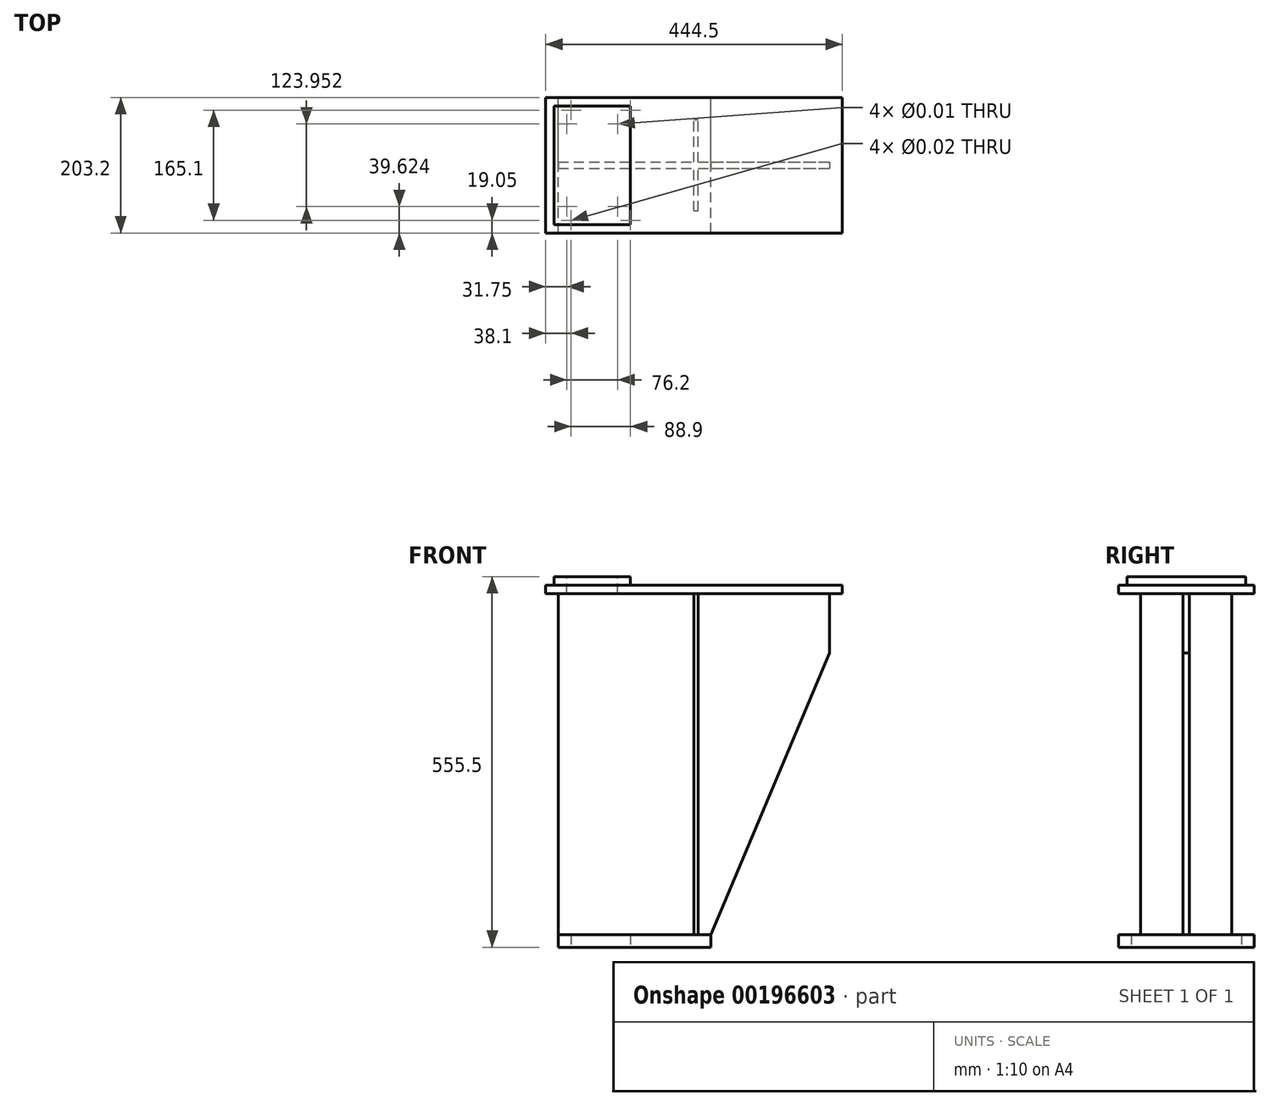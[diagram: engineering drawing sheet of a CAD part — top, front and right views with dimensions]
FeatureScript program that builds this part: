
annotation { "Feature Type Name" : "Feature", "Feature Type Description" : "" }
export const myFeature = defineFeature(function(context is Context, id is Id, definition is map)
    precondition{}
    {
        {
            var Q0;
            Q0=qCreatedBy(makeId("Top.planeOp"),FACE);
            var sketch = newSketch(context, id + "F0", { "sketchPlane" : qUnion([Q0])});
            skLineSegment(sketch, "E0.bottom", {"start": v(-222.25, 101.6) * mm, "end": v(222.25, 101.6) * mm});
            skLineSegment(sketch, "E0.top", {"start": v(-222.25, -101.6) * mm, "end": v(222.25, -101.6) * mm});
            skLineSegment(sketch, "E0.left", {"start": v(-222.25, 101.6) * mm, "end": v(-222.25, -101.6) * mm});
            skLineSegment(sketch, "E0.right", {"start": v(222.25, 101.6) * mm, "end": v(222.25, -101.6) * mm});
            skPoint(sketch, "E0.middle", {"position": v(0, 0) * mm});
            skSolve(sketch);
        }
        {
            var Q0;
            Q0 = qSketchRegion(id + "F0", true);
            extrude(context, id + "F1", {"entities" : qUnion([Q0]), "depth" : 12.7 * mm});
        }
        {
            var Q0;
            Q0=makeQuery(id+"F1.opExtrude","CAP_FACE",FACE,{"disambiguationData":[OSD([sQuery(id+"F0.wireOp",EDGE,"E0.bottom"),sQuery(id+"F0.wireOp",EDGE,"E0.top"),sQuery(id+"F0.wireOp",EDGE,"E0.left"),sQuery(id+"F0.wireOp",EDGE,"E0.right")])],"isStart":false});
            var sketch = newSketch(context, id + "F2", { "sketchPlane" : qUnion([Q0])});
            skLineSegment(sketch, "E1", {"start": v(-249.9, 0) * mm, "end": v(312.08, 0) * mm, "construction": true});
            skPoint(sketch, "E1.endSnap0", {"position": v(-222.25, 0) * mm});
            skLineSegment(sketch, "E2.0", {"start": v(-222.25, 101.6) * mm, "end": v(-222.25, -101.6) * mm, "construction": true});
            skLineSegment(sketch, "E3.0", {"start": v(-152.4, 101.6) * mm, "end": v(-152.4, -101.6) * mm, "construction": true});
            skLineSegment(sketch, "E4.0", {"start": v(-249.9, -88.9) * mm, "end": v(312.08, -88.9) * mm, "construction": true});
            skLineSegment(sketch, "E5.0", {"start": v(-209.55, 101.6) * mm, "end": v(-209.55, -101.6) * mm, "construction": true});
            skLineSegment(sketch, "E6.bottom", {"start": v(-209.55, -88.9) * mm, "end": v(-95.25, -88.9) * mm});
            skLineSegment(sketch, "E6.top", {"start": v(-209.55, 88.9) * mm, "end": v(-95.25, 88.9) * mm});
            skLineSegment(sketch, "E6.left", {"start": v(-209.55, -88.9) * mm, "end": v(-209.55, 88.9) * mm});
            skLineSegment(sketch, "E6.right", {"start": v(-95.25, -88.9) * mm, "end": v(-95.25, 88.9) * mm});
            skSolve(sketch);
        }
        {
            var Q0;
            Q0 = qSketchRegion(id + "F2", true);
            extrude(context, id + "F3", {"entities" : qUnion([Q0]), "operationType" : NewBodyOperationType.ADD, "depth" : 12.7 * mm});
        }
        {
            var Q0;
            Q0=makeQuery(id+"F3.opExtrude","CAP_FACE",FACE,{"disambiguationData":[OSD([sQuery(id+"F2.wireOp",EDGE,"E6.bottom"),sQuery(id+"F2.wireOp",EDGE,"E6.top"),sQuery(id+"F2.wireOp",EDGE,"E6.left"),sQuery(id+"F2.wireOp",EDGE,"E6.right")])],"isStart":false});
            var sketch = newSketch(context, id + "F4", { "sketchPlane" : qUnion([Q0])});
            skLineSegment(sketch, "E7", {"start": v(-266.4, 0) * mm, "end": v(-62.42, 0) * mm, "construction": true});
            skPoint(sketch, "E7.endSnap0", {"position": v(-95.25, 0) * mm});
            skLineSegment(sketch, "E8", {"start": v(-152.4, 88.9) * mm, "end": v(-152.4, -88.9) * mm, "construction": true});
            skLineSegment(sketch, "E9.0", {"start": v(-190.5, 88.9) * mm, "end": v(-190.5, -88.9) * mm, "construction": true});
            skLineSegment(sketch, "E10.0", {"start": v(-266.4, 61.98) * mm, "end": v(-62.42, 61.98) * mm, "construction": true});
            skPoint(sketch, "E11", {"position": v(-190.5, 61.98) * mm});
            skPoint(sketch, "E12.0.1.0", {"position": v(-190.5, -61.98) * mm});
            skPoint(sketch, "E12.1.0.0", {"position": v(-114.3, 61.98) * mm});
            skPoint(sketch, "E12.1.1.0", {"position": v(-114.3, -61.98) * mm});
            skLineSegment(sketch, "E12.direction1", {"start": v(-190.5, 61.98) * mm, "end": v(-114.3, 61.98) * mm, "construction": true});
            skLineSegment(sketch, "E12.direction2", {"start": v(-190.5, 61.98) * mm, "end": v(-190.5, -61.98) * mm, "construction": true});
            skSolve(sketch);
        }
        {
            var Q0;
            Q0=sQuery(id+"F4.wireOp",VERTEX,"E11");
            var Q1;
            Q1=sQuery(id+"F4.wireOp",VERTEX,"E12.1.0.0");
            var Q2;
            Q2=sQuery(id+"F4.wireOp",VERTEX,"E12.1.1.0");
            var Q3;
            Q3=sQuery(id+"F4.wireOp",VERTEX,"E12.0.1.0");
            var Q4;
            Q4=makeQuery(id+"F1.opExtrude","SWEPT_BODY",BODY,{"disambiguationData":[OSD([sQuery(id+"F0.wireOp",EDGE,"E0.bottom"),sQuery(id+"F0.wireOp",EDGE,"E0.top"),sQuery(id+"F0.wireOp",EDGE,"E0.left"),sQuery(id+"F0.wireOp",EDGE,"E0.right")])]});
            hole(context, id + "F5", {"style" : HoleStyle.SIMPLE, "endStyle" : HoleEndStyle.THROUGH, "standardTappedOrClearance" : lookupTablePath({ "standard" : "ANSI", "size" : "3/8 (0.38)", "type" : "Drilled" }), "standardBlindInLast" : lookupTablePath({ "standard" : "ANSI", "size" : "3/8", "type" : "Drilled" }), "holeDiameter" : 3 / 203.2 * mm, "locations" : qUnion([Q0, Q1, Q2, Q3]), "scope" : qUnion([Q4]), "isTappedThrough" : true});
        }
        {
            var Q0;
            Q0=makeQuery(id+"F1.opExtrude","CAP_FACE",FACE,{"disambiguationData":[OSD([sQuery(id+"F0.wireOp",EDGE,"E0.bottom"),sQuery(id+"F0.wireOp",EDGE,"E0.top"),sQuery(id+"F0.wireOp",EDGE,"E0.left"),sQuery(id+"F0.wireOp",EDGE,"E0.right")])],"isStart":true});
            var sketch = newSketch(context, id + "F6", { "sketchPlane" : qUnion([Q0])});
            skLineSegment(sketch, "E13.0", {"start": v(-222.25, -101.6) * mm, "end": v(-222.25, 101.6) * mm, "construction": true});
            skLineSegment(sketch, "E14.0", {"start": v(-203.2, -101.6) * mm, "end": v(-203.2, 101.6) * mm, "construction": true});
            skLineSegment(sketch, "E15", {"start": v(-293.96, 0) * mm, "end": v(264.65, 0) * mm, "construction": true});
            skLineSegment(sketch, "E16.0", {"start": v(-293.96, -4.83) * mm, "end": v(264.65, -4.83) * mm, "construction": true});
            skLineSegment(sketch, "E17.bottom", {"start": v(-203.2, -4.83) * mm, "end": v(203.2, -4.83) * mm});
            skLineSegment(sketch, "E17.top", {"start": v(-203.2, 4.83) * mm, "end": v(203.2, 4.83) * mm});
            skLineSegment(sketch, "E17.left", {"start": v(-203.2, -4.83) * mm, "end": v(-203.2, 4.83) * mm});
            skLineSegment(sketch, "E17.right", {"start": v(203.2, -4.83) * mm, "end": v(203.2, 4.83) * mm});
            skLineSegment(sketch, "E18.0", {"start": v(0, -101.6) * mm, "end": v(0, 101.6) * mm, "construction": true});
            skLineSegment(sketch, "E19.bottom", {"start": v(0, 68.33) * mm, "end": v(6.35, 68.33) * mm});
            skLineSegment(sketch, "E19.top", {"start": v(0, -68.33) * mm, "end": v(6.35, -68.33) * mm});
            skLineSegment(sketch, "E19.left", {"start": v(0, 68.33) * mm, "end": v(0, -68.33) * mm});
            skLineSegment(sketch, "E19.right", {"start": v(6.35, 68.33) * mm, "end": v(6.35, -68.33) * mm});
            skSolve(sketch);
        }
        {
            var Q0;
            Q0 = qSketchRegion(id + "F6", true);
            extrude(context, id + "F7", {"entities" : qUnion([Q0]), "operationType" : NewBodyOperationType.ADD, "depth" : 511.05 * mm});
        }
        {
            var Q0;
            {var subQ0=sQuery(id+"F6.wireOp",EDGE,"E17.top");Q0=makeQuery(id+"F7.opExtrude","SWEPT_FACE",FACE,{"disambiguationData":[OSD([subQ0]),TDD([makeQuery(id+"F6.imprint","IMPRINT",EDGE,{"disambiguationData":[TD([[makeQuery(id+"F6.imprint","INTERSECT",VERTEX,{"derivedFrom":[subQ0,sQuery(id+"F6.wireOp",EDGE,"E17.right")]}),1.0]])],"derivedFrom":subQ0})])]});}
            var sketch = newSketch(context, id + "F8", { "sketchPlane" : qUnion([Q0])});
            skLineSegment(sketch, "E20.0", {"start": v(-222.25, 0) * mm, "end": v(222.25, 0) * mm, "construction": true});
            skLineSegment(sketch, "E21.0", {"start": v(-203.2, -511.05) * mm, "end": v(-203.2, 0) * mm, "construction": true});
            skLineSegment(sketch, "E22.0", {"start": v(25.4, -511.05) * mm, "end": v(25.4, 0) * mm, "construction": true});
            skLineSegment(sketch, "E23.0", {"start": v(-222.25, -88.9) * mm, "end": v(222.25, -88.9) * mm, "construction": true});
            skLineSegment(sketch, "E24", {"start": v(25.4, -511.05) * mm, "end": v(203.2, -88.9) * mm});
            skLineSegment(sketch, "E25", {"start": v(203.2, -88.9) * mm, "end": v(203.2, -511.05) * mm});
            skLineSegment(sketch, "E26", {"start": v(203.2, -511.05) * mm, "end": v(25.4, -511.05) * mm});
            skSolve(sketch);
        }
        {
            var Q0;
            Q0 = qSketchRegion(id + "F8", true);
            extrude(context, id + "F9", {"entities" : qUnion([Q0]), "operationType" : NewBodyOperationType.REMOVE, "endBound" : BoundingType.THROUGH_ALL, "oppositeDirection" : true, "depth" : 25.4 * mm});
        }
        {
            var Q0;
            Q0=makeQuery(id+"F7.opExtrude","CAP_FACE",FACE,{"disambiguationData":[OSD([sQuery(id+"F6.wireOp",EDGE,"E17.bottom"),sQuery(id+"F6.wireOp",EDGE,"E17.top"),sQuery(id+"F6.wireOp",EDGE,"E17.left"),sQuery(id+"F6.wireOp",EDGE,"E17.right"),sQuery(id+"F6.wireOp",EDGE,"E19.bottom"),sQuery(id+"F6.wireOp",EDGE,"E19.top"),sQuery(id+"F6.wireOp",EDGE,"E19.left"),sQuery(id+"F6.wireOp",EDGE,"E19.right")])],"isStart":false});
            var sketch = newSketch(context, id + "F10", { "sketchPlane" : qUnion([Q0])});
            skLineSegment(sketch, "E27.bottom", {"start": v(-203.2, 101.6) * mm, "end": v(25.4, 101.6) * mm});
            skLineSegment(sketch, "E27.top", {"start": v(-203.2, -101.6) * mm, "end": v(25.4, -101.6) * mm});
            skLineSegment(sketch, "E27.left", {"start": v(-203.2, 101.6) * mm, "end": v(-203.2, -101.6) * mm});
            skLineSegment(sketch, "E27.right", {"start": v(25.4, 101.6) * mm, "end": v(25.4, -101.6) * mm});
            skSolve(sketch);
        }
        {
            var Q0;
            Q0 = qSketchRegion(id + "F10", true);
            extrude(context, id + "F11", {"entities" : qUnion([Q0]), "operationType" : NewBodyOperationType.ADD, "depth" : 19.05 * mm});
        }
        {
            var Q0;
            Q0=makeQuery(id+"F11.opExtrude","CAP_FACE",FACE,{"disambiguationData":[OSD([sQuery(id+"F10.wireOp",EDGE,"E27.bottom"),sQuery(id+"F10.wireOp",EDGE,"E27.top"),sQuery(id+"F10.wireOp",EDGE,"E27.left"),sQuery(id+"F10.wireOp",EDGE,"E27.right")])],"isStart":false});
            var sketch = newSketch(context, id + "F12", { "sketchPlane" : qUnion([Q0])});
            skLineSegment(sketch, "E28.0", {"start": v(-203.2, 101.6) * mm, "end": v(-203.2, -101.6) * mm, "construction": true});
            skLineSegment(sketch, "E29.0", {"start": v(-184.15, 101.6) * mm, "end": v(-184.15, -101.6) * mm, "construction": true});
            skLineSegment(sketch, "E30.0", {"start": v(-95.25, 101.6) * mm, "end": v(-95.25, -101.6) * mm, "construction": true});
            skLineSegment(sketch, "E31", {"start": v(-95.25, 0) * mm, "end": v(-277.82, 0) * mm, "construction": true});
            skLineSegment(sketch, "E32.0", {"start": v(-95.25, 82.55) * mm, "end": v(-277.82, 82.55) * mm, "construction": true});
            skPoint(sketch, "E33", {"position": v(-184.15, 82.55) * mm});
            skPoint(sketch, "E34", {"position": v(-95.25, 82.55) * mm});
            skPoint(sketch, "E35.MirrorP", {"position": v(-184.15, -82.55) * mm});
            skPoint(sketch, "E36.MirrorP", {"position": v(-95.25, -82.55) * mm});
            skSolve(sketch);
        }
        {
            var Q0;
            Q0=sQuery(id+"F12.wireOp",VERTEX,"E33");
            var Q1;
            Q1=sQuery(id+"F12.wireOp",VERTEX,"E34");
            var Q2;
            Q2=sQuery(id+"F12.wireOp",VERTEX,"E36.MirrorP");
            var Q3;
            Q3=sQuery(id+"F12.wireOp",VERTEX,"E35.MirrorP");
            var Q4;
            Q4=makeQuery(id+"F1.opExtrude","SWEPT_BODY",BODY,{"disambiguationData":[OSD([sQuery(id+"F0.wireOp",EDGE,"E0.bottom"),sQuery(id+"F0.wireOp",EDGE,"E0.top"),sQuery(id+"F0.wireOp",EDGE,"E0.left"),sQuery(id+"F0.wireOp",EDGE,"E0.right")])]});
            hole(context, id + "F13", {"style" : HoleStyle.SIMPLE, "endStyle" : HoleEndStyle.BLIND, "standardTappedOrClearance" : lookupTablePath({ "standard" : "ANSI", "size" : "9/16 (0.56)", "type" : "Drilled" }), "standardBlindInLast" : lookupTablePath({ "standard" : "ANSI", "size" : "9/16", "type" : "Drilled" }), "holeDiameter" : 9 / 406.4 * mm, "holeDepth" : 31.75 * mm, "locations" : qUnion([Q0, Q1, Q2, Q3]), "scope" : qUnion([Q4])});
        }
    });
